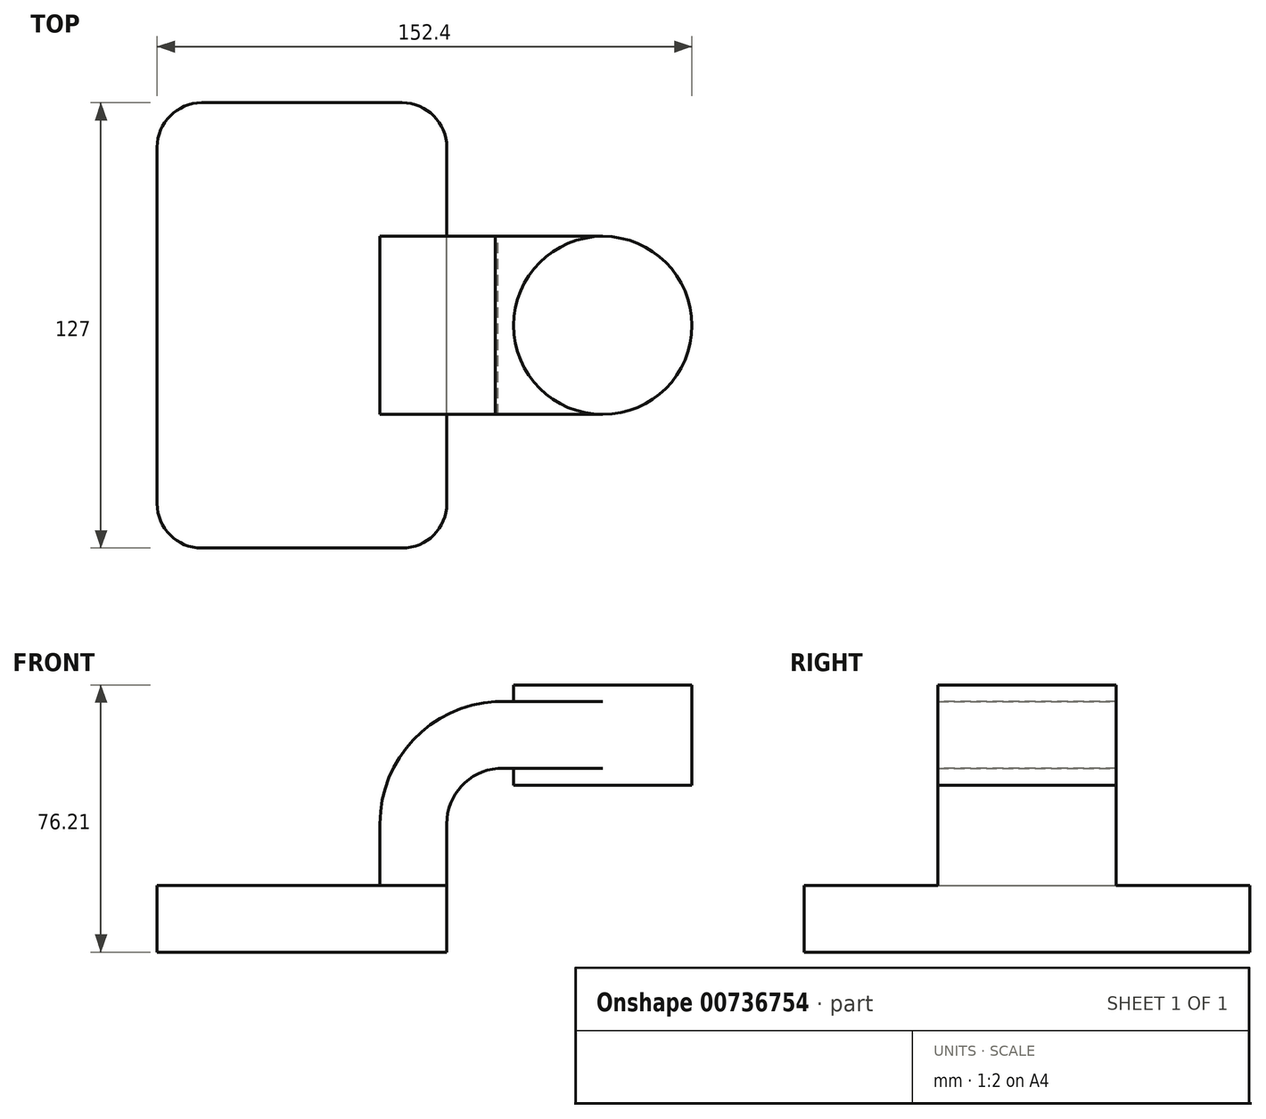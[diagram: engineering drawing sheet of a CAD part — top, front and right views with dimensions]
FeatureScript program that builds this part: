
annotation { "Feature Type Name" : "Feature", "Feature Type Description" : "" }
export const myFeature = defineFeature(function(context is Context, id is Id, definition is map)
    precondition{}
    {
        {
            var Q0;
            Q0=qCreatedBy(makeId("Front.planeOp"),FACE);
            var sketch = newSketch(context, id + "F0", { "sketchPlane" : qUnion([Q0])});
            skLineSegment(sketch, "E0.bottom", {"start": v(-41.28, 9.52) * mm, "end": v(41.27, 9.53) * mm});
            skLineSegment(sketch, "E0.top", {"start": v(-41.28, -9.53) * mm, "end": v(41.28, -9.53) * mm});
            skLineSegment(sketch, "E0.left", {"start": v(-41.28, 9.52) * mm, "end": v(-41.27, -9.53) * mm});
            skLineSegment(sketch, "E0.right", {"start": v(41.28, 9.53) * mm, "end": v(41.28, -9.52) * mm});
            skPoint(sketch, "E0.middle", {"position": v(0, 0) * mm});
            skLineSegment(sketch, "E1", {"start": v(41.27, 9.53) * mm, "end": v(41.27, 27.06) * mm});
            skArc(sketch, "E2", {"start": v(41.27, 27.06) * mm, "mid": v(45.46, 37.8) * mm, "end": v(55.8, 42.88) * mm});
            skLineSegment(sketch, "E3.bottom", {"start": v(60.32, 66.67) * mm, "end": v(111.12, 66.67) * mm});
            skLineSegment(sketch, "E3.top", {"start": v(60.32, 38.1) * mm, "end": v(111.12, 38.1) * mm});
            skLineSegment(sketch, "E3.left", {"start": v(60.32, 66.67) * mm, "end": v(60.32, 38.1) * mm});
            skLineSegment(sketch, "E3.right", {"start": v(111.12, 66.67) * mm, "end": v(111.12, 38.1) * mm});
            skPoint(sketch, "E3.middle", {"position": v(85.72, 52.39) * mm});
            skLineSegment(sketch, "E4", {"start": v(55.8, 42.88) * mm, "end": v(85.72, 42.88) * mm});
            skLineSegment(sketch, "E5.0", {"start": v(55.15, 61.93) * mm, "end": v(85.72, 61.93) * mm});
            skArc(sketch, "E5.1", {"start": v(22.23, 27.06) * mm, "mid": v(31.76, 51.03) * mm, "end": v(55.15, 61.93) * mm});
            skLineSegment(sketch, "E5.2", {"start": v(22.22, 9.53) * mm, "end": v(22.22, 27.06) * mm});
            skLineSegment(sketch, "E6", {"start": v(85.72, 61.93) * mm, "end": v(85.72, 42.88) * mm});
            skFitSpline(sketch, "E7", {"points": [v(-41.28, 9.52) * mm, v(55.15, 61.93) * mm], "startDerivative": vector(11.98, 101.34) * mm, "endDerivative": vector(193.17, 0.07) * mm});
            skLineSegment(sketch, "E8", {"start": v(85.72, 61.93) * mm, "end": v(85.72, 66.67) * mm});
            skLineSegment(sketch, "E9", {"start": v(85.72, 66.67) * mm, "end": v(85.72, 42.88) * mm});
            skLineSegment(sketch, "E10", {"start": v(85.72, 38.1) * mm, "end": v(85.72, 42.88) * mm});
            skSolve(sketch);
        }
        {
            var Q0;
            Q0=makeQuery(id+"F0.imprint","IMPRINT",FACE,{"disambiguationData":[TD([[makeQuery(id+"F0.imprint","IMPRINT",EDGE,{"derivedFrom":sQuery(id+"F0.wireOp",EDGE,"E0.top")}),1.0]])]});
            extrude(context, id + "F1", {"entities" : qUnion([Q0]), "endBound" : BoundingType.SYMMETRIC, "depth" : 127 * mm, "offsetDistance" : 25.4 * mm});
        }
        {
            var Q0;
            {var subQ5=sQuery(id+"F0.wireOp",EDGE,"E1");Q0=makeQuery(id+"F0.imprint","IMPRINT",FACE,{"disambiguationData":[TD([[makeQuery(id+"F0.imprint","IMPRINT",EDGE,{"derivedFrom":subQ5}),1.0]])]});}
            var Q1;
            {var subQ0=sQuery(id+"F0.wireOp",EDGE,"E5.0");var subQ1=sQuery(id+"F0.wireOp",EDGE,"E3.left");var subQ2=makeQuery(id+"F0.imprint","INTERSECT",VERTEX,{"derivedFrom":[subQ1,subQ0]});Q1=makeQuery(id+"F0.imprint","IMPRINT",FACE,{"disambiguationData":[TD([[makeQuery(id+"F0.imprint","IMPRINT",EDGE,{"disambiguationData":[TD([[subQ2,-1.0]])],"derivedFrom":subQ1}),1.0]])]});}
            extrude(context, id + "F2", {"entities" : qUnion([Q0, Q1]), "operationType" : NewBodyOperationType.ADD, "endBound" : BoundingType.SYMMETRIC, "depth" : 50.8 * mm, "offsetDistance" : 25.4 * mm});
        }
        {
            var Q0;
            Q0=makeQuery(id+"F0.imprint","IMPRINT",FACE,{"disambiguationData":[TD([[makeQuery(id+"F0.imprint","IMPRINT",EDGE,{"derivedFrom":sQuery(id+"F0.wireOp",EDGE,"E5.1")}),1.0]])]});
            extrude(context, id + "F3", {"entities" : qUnion([Q0]), "operationType" : NewBodyOperationType.ADD, "endBound" : BoundingType.SYMMETRIC, "depth" : 15.88 * mm, "offsetDistance" : 25.4 * mm});
        }
        {
            var Q0;
            {var subQ4=sQuery(id+"F0.wireOp",EDGE,"E3.right");Q0=makeQuery(id+"F0.imprint","IMPRINT",FACE,{"disambiguationData":[TD([[makeQuery(id+"F0.imprint","IMPRINT",EDGE,{"derivedFrom":subQ4}),-1.0]])]});}
            var Q1;
            Q1=sQuery(id+"F0.wireOp",EDGE,"E6");
            revolve(context, id + "F4", {"operationType" : NewBodyOperationType.ADD, "surfaceOperationType" : NewSurfaceOperationType.NEW, "entities" : qUnion([Q0]), "axis" : qUnion([Q1]), "revolveType" : RevolveType.FULL});
        }
        {
            var Q0;
            Q0=makeQuery(id+"F1.opExtrude","CAP_EDGE",EDGE,{"disambiguationData":[OSD([sQuery(id+"F0.wireOp",EDGE,"E0.right")])],"isStart":false});
            var Q1;
            Q1=makeQuery(id+"F1.opExtrude","CAP_EDGE",EDGE,{"disambiguationData":[OSD([sQuery(id+"F0.wireOp",EDGE,"E0.left")])],"isStart":false});
            var Q2;
            Q2=makeQuery(id+"F1.opExtrude","CAP_EDGE",EDGE,{"disambiguationData":[OSD([sQuery(id+"F0.wireOp",EDGE,"E0.right")])],"isStart":true});
            var Q3;
            Q3=makeQuery(id+"F1.opExtrude","CAP_EDGE",EDGE,{"disambiguationData":[OSD([sQuery(id+"F0.wireOp",EDGE,"E0.left")])],"isStart":true});
            fillet(context, id + "F5", {"entities" : qUnion([Q0, Q1, Q2, Q3]), "radius" : 12.7 * mm, "tangentPropagation" : true, "allowEdgeOverflow" : false});
        }
    });
